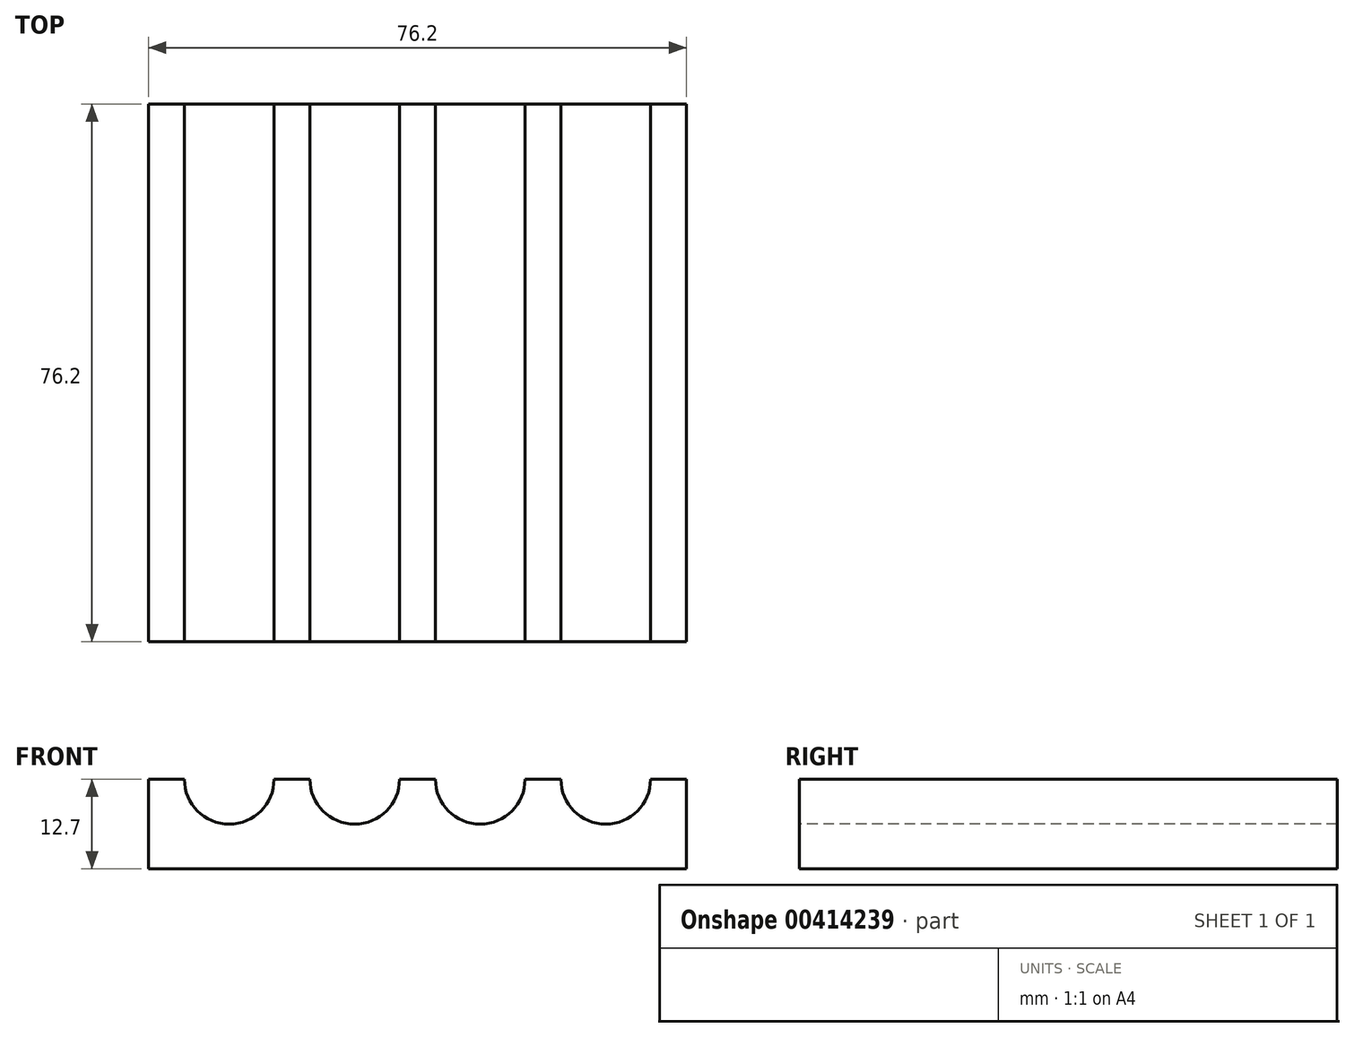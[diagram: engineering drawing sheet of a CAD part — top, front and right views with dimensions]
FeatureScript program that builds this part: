
annotation { "Feature Type Name" : "Feature", "Feature Type Description" : "" }
export const myFeature = defineFeature(function(context is Context, id is Id, definition is map)
    precondition{}
    {
        {
            var Q0;
            Q0=qCreatedBy(makeId("Top.planeOp"),FACE);
            var sketch = newSketch(context, id + "F0", { "sketchPlane" : qUnion([Q0])});
            skLineSegment(sketch, "E0.bottom", {"start": v(0, 0) * mm, "end": v(76.2, 0) * mm});
            skLineSegment(sketch, "E0.top", {"start": v(0, 76.2) * mm, "end": v(76.2, 76.2) * mm});
            skLineSegment(sketch, "E0.left", {"start": v(0, 0) * mm, "end": v(0, 76.2) * mm});
            skLineSegment(sketch, "E0.right", {"start": v(76.2, 0) * mm, "end": v(76.2, 76.2) * mm});
            skSolve(sketch);
        }
        {
            var Q0;
            Q0=makeQuery(id+"F0.imprint","IMPRINT",FACE,{"disambiguationData":[TD([[makeQuery(id+"F0.imprint","IMPRINT",EDGE,{"derivedFrom":sQuery(id+"F0.wireOp",EDGE,"E0.bottom")}),1.0]])]});
            extrude(context, id + "F1", {"entities" : qUnion([Q0]), "depth" : 12.7 * mm, "offsetDistance" : 25.4 * mm});
        }
        {
            var Q0;
            Q0=makeQuery(id+"F1.opExtrude","SWEPT_FACE",FACE,{"disambiguationData":[OSD([sQuery(id+"F0.wireOp",EDGE,"E0.bottom")])]});
            var sketch = newSketch(context, id + "F2", { "sketchPlane" : qUnion([Q0])});
            skCircle(sketch, "E1", {"center": v(11.43, 12.7) * mm, "radius": 6.35 * mm});
            skCircle(sketch, "E2.1.0.0", {"center": v(29.21, 12.7) * mm, "radius": 6.35 * mm});
            skCircle(sketch, "E2.2.0.0", {"center": v(46.99, 12.7) * mm, "radius": 6.35 * mm});
            skCircle(sketch, "E2.3.0.0", {"center": v(64.77, 12.7) * mm, "radius": 6.35 * mm});
            skLineSegment(sketch, "E2.direction1", {"start": v(11.43, 12.7) * mm, "end": v(29.21, 12.7) * mm, "construction": true});
            skSolve(sketch);
        }
        {
            var Q0;
            {var subQ0=sQuery(id+"F2.wireOp",EDGE,"E1");var subQ1=makeQuery(id+"F1.opExtrude","CAP_EDGE",EDGE,{"disambiguationData":[OSD([sQuery(id+"F0.wireOp",EDGE,"E0.bottom")])],"isStart":false});var subQ2=makeQuery(id+"F2.imprint","INTERSECT",VERTEX,{"disambiguationData":[OD(0.0)],"derivedFrom":[subQ1,subQ0]});Q0=makeQuery(id+"F2.imprint","IMPRINT",FACE,{"disambiguationData":[TD([[makeQuery(id+"F2.imprint","IMPRINT",EDGE,{"disambiguationData":[TD([[subQ2,-1.0]])],"derivedFrom":subQ0}),1.0]])]});}
            var Q1;
            {var subQ0=sQuery(id+"F2.wireOp",EDGE,"E2.1.0.0");var subQ1=makeQuery(id+"F1.opExtrude","CAP_EDGE",EDGE,{"disambiguationData":[OSD([sQuery(id+"F0.wireOp",EDGE,"E0.bottom")])],"isStart":false});var subQ2=makeQuery(id+"F2.imprint","INTERSECT",VERTEX,{"disambiguationData":[OD(0.0)],"derivedFrom":[subQ1,subQ0]});Q1=makeQuery(id+"F2.imprint","IMPRINT",FACE,{"disambiguationData":[TD([[makeQuery(id+"F2.imprint","IMPRINT",EDGE,{"disambiguationData":[TD([[subQ2,-1.0]])],"derivedFrom":subQ0}),1.0]])]});}
            var Q2;
            {var subQ0=sQuery(id+"F2.wireOp",EDGE,"E2.2.0.0");var subQ1=makeQuery(id+"F1.opExtrude","CAP_EDGE",EDGE,{"disambiguationData":[OSD([sQuery(id+"F0.wireOp",EDGE,"E0.bottom")])],"isStart":false});var subQ2=makeQuery(id+"F2.imprint","INTERSECT",VERTEX,{"disambiguationData":[OD(0.0)],"derivedFrom":[subQ1,subQ0]});Q2=makeQuery(id+"F2.imprint","IMPRINT",FACE,{"disambiguationData":[TD([[makeQuery(id+"F2.imprint","IMPRINT",EDGE,{"disambiguationData":[TD([[subQ2,1.0]])],"derivedFrom":subQ0}),1.0]])]});}
            var Q3;
            {var subQ0=sQuery(id+"F2.wireOp",EDGE,"E2.3.0.0");var subQ1=makeQuery(id+"F1.opExtrude","CAP_EDGE",EDGE,{"disambiguationData":[OSD([sQuery(id+"F0.wireOp",EDGE,"E0.bottom")])],"isStart":false});var subQ2=makeQuery(id+"F2.imprint","INTERSECT",VERTEX,{"disambiguationData":[OD(0.0)],"derivedFrom":[subQ1,subQ0]});Q3=makeQuery(id+"F2.imprint","IMPRINT",FACE,{"disambiguationData":[TD([[makeQuery(id+"F2.imprint","IMPRINT",EDGE,{"disambiguationData":[TD([[subQ2,1.0]])],"derivedFrom":subQ0}),1.0]])]});}
            extrude(context, id + "F3", {"entities" : qUnion([Q0, Q1, Q2, Q3]), "operationType" : NewBodyOperationType.REMOVE, "endBound" : BoundingType.THROUGH_ALL, "oppositeDirection" : true, "depth" : 25.4 * mm, "offsetDistance" : 25.4 * mm});
        }
    });
